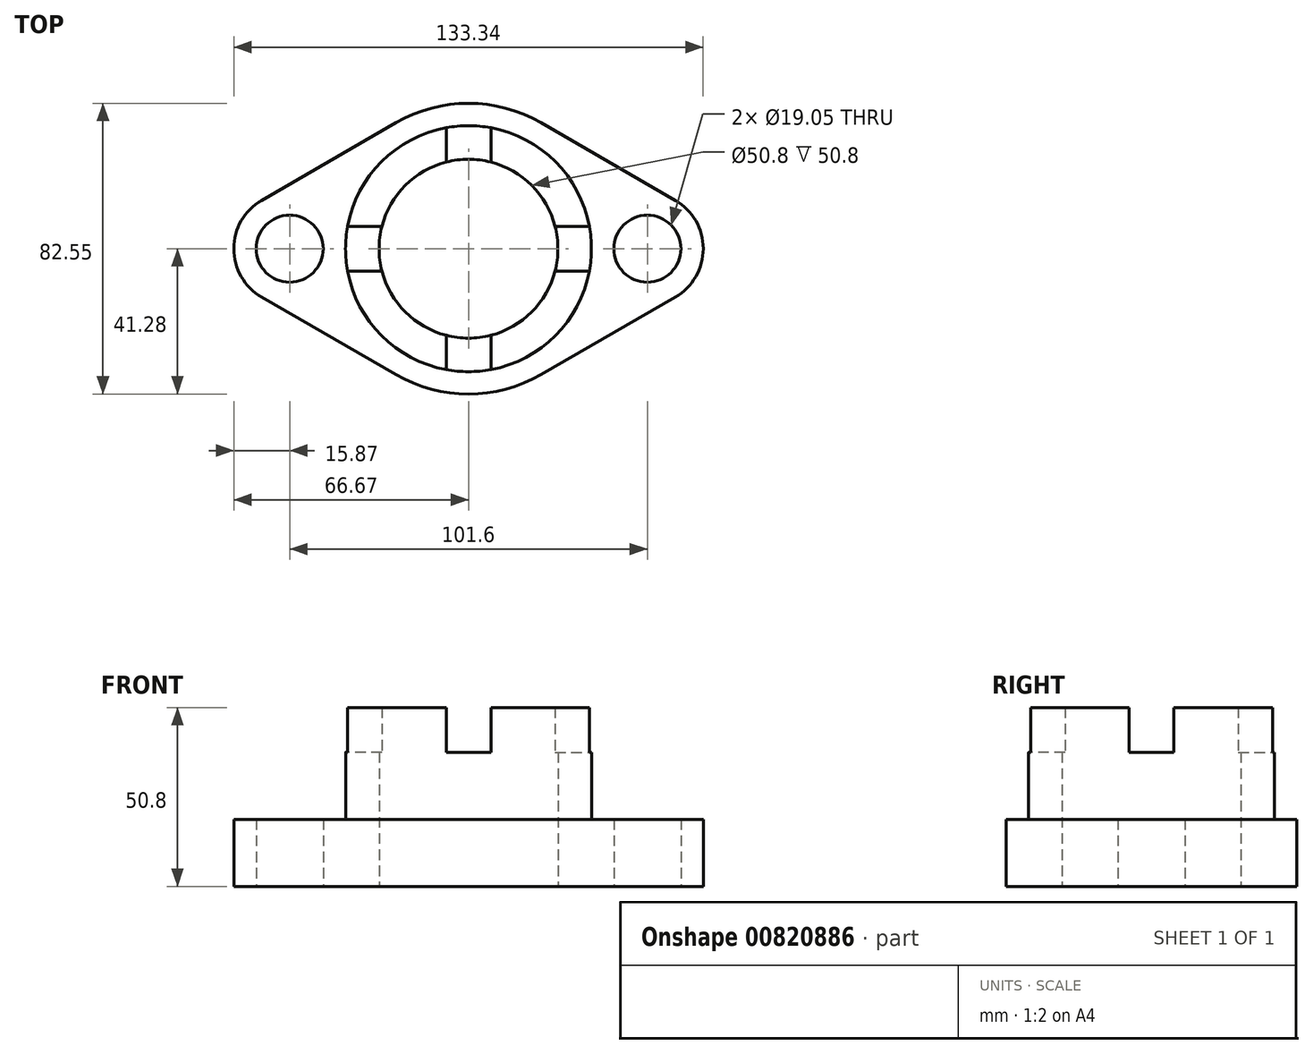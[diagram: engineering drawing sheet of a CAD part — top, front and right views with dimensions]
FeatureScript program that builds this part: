
annotation { "Feature Type Name" : "Feature", "Feature Type Description" : "" }
export const myFeature = defineFeature(function(context is Context, id is Id, definition is map)
    precondition{}
    {
        {
            var Q0;
            Q0=qCreatedBy(makeId("Top.planeOp"),FACE);
            var sketch = newSketch(context, id + "F0", { "sketchPlane" : qUnion([Q0])});
            skCircle(sketch, "E0", {"center": v(0, 0) * mm, "radius": 12.7 * mm});
            skCircle(sketch, "E1", {"center": v(-50.8, 0) * mm, "radius": 9.53 * mm});
            skCircle(sketch, "E2", {"center": v(0, 0) * mm, "radius": 25.4 * mm});
            skCircle(sketch, "E3", {"center": v(0, 0) * mm, "radius": 34.93 * mm});
            skLineSegment(sketch, "E4", {"start": v(-34.34, -6.35) * mm, "end": v(-24.6, -6.35) * mm});
            skLineSegment(sketch, "E5", {"start": v(-34.34, 6.35) * mm, "end": v(-24.6, 6.35) * mm});
            skLineSegment(sketch, "E6", {"start": v(-6.35, 34.34) * mm, "end": v(-6.35, 24.6) * mm});
            skLineSegment(sketch, "E7", {"start": v(-6.35, -34.34) * mm, "end": v(-6.35, -24.6) * mm});
            skLineSegment(sketch, "E8.MirrorCS", {"start": v(34.34, 6.35) * mm, "end": v(24.6, 6.35) * mm});
            skLineSegment(sketch, "E9.MirrorCS", {"start": v(6.35, -34.34) * mm, "end": v(6.35, -24.6) * mm});
            skLineSegment(sketch, "E10.MirrorCS", {"start": v(6.35, 34.34) * mm, "end": v(6.35, 24.6) * mm});
            skLineSegment(sketch, "E11.MirrorCS", {"start": v(34.34, -6.35) * mm, "end": v(24.6, -6.35) * mm});
            skCircle(sketch, "E12.MirrorC", {"center": v(50.8, 0) * mm, "radius": 9.53 * mm});
            skArc(sketch, "E13", {"start": v(58.74, -13.75) * mm, "mid": v(66.68, 0) * mm, "end": v(58.74, 13.75) * mm});
            skArc(sketch, "E14", {"start": v(-58.74, 13.75) * mm, "mid": v(-66.68, 0) * mm, "end": v(-58.74, -13.75) * mm});
            skLineSegment(sketch, "E15", {"start": v(-58.74, -13.75) * mm, "end": v(-20.64, -35.75) * mm});
            skLineSegment(sketch, "E16", {"start": v(-58.74, 13.75) * mm, "end": v(-20.64, 35.75) * mm});
            skLineSegment(sketch, "E17", {"start": v(20.64, -35.75) * mm, "end": v(58.74, -13.75) * mm});
            skLineSegment(sketch, "E18", {"start": v(20.64, 35.75) * mm, "end": v(58.74, 13.75) * mm});
            skArc(sketch, "E19.trimOffspring", {"start": v(-20.64, -35.75) * mm, "mid": v(0, -41.28) * mm, "end": v(20.64, -35.75) * mm});
            skArc(sketch, "E20.trimOffspring", {"start": v(20.64, 35.75) * mm, "mid": v(0, 41.28) * mm, "end": v(-20.64, 35.75) * mm});
            skPoint(sketch, "E21.end.orphan", {"position": v(0, -6.35) * mm});
            skSolve(sketch);
        }
        {
            var Q0;
            Q0 = qSketchRegion(id + "F0", true);
            extrude(context, id + "F1", {"entities" : qUnion([Q0]), "depth" : 19.05 * mm, "offsetDistance" : 25.4 * mm});
        }
        {
            var Q0;
            {var subQ0=sQuery(id+"F0.wireOp",EDGE,"E7");Q0=makeQuery(id+"F0.imprint","IMPRINT",FACE,{"disambiguationData":[TD([[makeQuery(id+"F0.imprint","IMPRINT",EDGE,{"derivedFrom":subQ0}),-1.0]])]});}
            var Q1;
            {var subQ0=sQuery(id+"F0.wireOp",EDGE,"E4");Q1=makeQuery(id+"F0.imprint","IMPRINT",FACE,{"disambiguationData":[TD([[makeQuery(id+"F0.imprint","IMPRINT",EDGE,{"derivedFrom":subQ0}),-1.0]])]});}
            var Q2;
            {var subQ0=sQuery(id+"F0.wireOp",EDGE,"E9.MirrorCS");Q2=makeQuery(id+"F0.imprint","IMPRINT",FACE,{"disambiguationData":[TD([[makeQuery(id+"F0.imprint","IMPRINT",EDGE,{"derivedFrom":subQ0}),-1.0]])]});}
            var Q3;
            Q3=makeQuery(id+"F0.imprint","IMPRINT",FACE,{"disambiguationData":[TD([[makeQuery(id+"F0.imprint","IMPRINT",EDGE,{"derivedFrom":sQuery(id+"F0.wireOp",EDGE,"E0")}),1.0]])]});
            var Q4;
            {var subQ0=sQuery(id+"F0.wireOp",EDGE,"E8.MirrorCS");Q4=makeQuery(id+"F0.imprint","IMPRINT",FACE,{"disambiguationData":[TD([[makeQuery(id+"F0.imprint","IMPRINT",EDGE,{"derivedFrom":subQ0}),1.0]])]});}
            var Q5;
            {var subQ0=sQuery(id+"F0.wireOp",EDGE,"E8.MirrorCS");Q5=makeQuery(id+"F0.imprint","IMPRINT",FACE,{"disambiguationData":[TD([[makeQuery(id+"F0.imprint","IMPRINT",EDGE,{"derivedFrom":subQ0}),-1.0]])]});}
            var Q6;
            {var subQ0=sQuery(id+"F0.wireOp",EDGE,"E4");Q6=makeQuery(id+"F0.imprint","IMPRINT",FACE,{"disambiguationData":[TD([[makeQuery(id+"F0.imprint","IMPRINT",EDGE,{"derivedFrom":subQ0}),1.0]])]});}
            var Q7;
            {var subQ0=sQuery(id+"F0.wireOp",EDGE,"E5");Q7=makeQuery(id+"F0.imprint","IMPRINT",FACE,{"disambiguationData":[TD([[makeQuery(id+"F0.imprint","IMPRINT",EDGE,{"derivedFrom":subQ0}),1.0]])]});}
            var Q8;
            {var subQ0=sQuery(id+"F0.wireOp",EDGE,"E6");Q8=makeQuery(id+"F0.imprint","IMPRINT",FACE,{"disambiguationData":[TD([[makeQuery(id+"F0.imprint","IMPRINT",EDGE,{"derivedFrom":subQ0}),1.0]])]});}
            extrude(context, id + "F2", {"entities" : qUnion([Q0, Q1, Q2, Q3, Q4, Q5, Q6, Q7, Q8]), "operationType" : NewBodyOperationType.ADD, "depth" : 38.1 * mm, "offsetDistance" : 25.4 * mm});
        }
        {
            var Q0;
            {var subQ0=sQuery(id+"F0.wireOp",EDGE,"E8.MirrorCS");Q0=makeQuery(id+"F0.imprint","IMPRINT",FACE,{"disambiguationData":[TD([[makeQuery(id+"F0.imprint","IMPRINT",EDGE,{"derivedFrom":subQ0}),-1.0]])]});}
            var Q1;
            {var subQ0=sQuery(id+"F0.wireOp",EDGE,"E9.MirrorCS");Q1=makeQuery(id+"F0.imprint","IMPRINT",FACE,{"disambiguationData":[TD([[makeQuery(id+"F0.imprint","IMPRINT",EDGE,{"derivedFrom":subQ0}),-1.0]])]});}
            var Q2;
            {var subQ0=sQuery(id+"F0.wireOp",EDGE,"E4");Q2=makeQuery(id+"F0.imprint","IMPRINT",FACE,{"disambiguationData":[TD([[makeQuery(id+"F0.imprint","IMPRINT",EDGE,{"derivedFrom":subQ0}),-1.0]])]});}
            var Q3;
            {var subQ0=sQuery(id+"F0.wireOp",EDGE,"E5");Q3=makeQuery(id+"F0.imprint","IMPRINT",FACE,{"disambiguationData":[TD([[makeQuery(id+"F0.imprint","IMPRINT",EDGE,{"derivedFrom":subQ0}),1.0]])]});}
            extrude(context, id + "F3", {"entities" : qUnion([Q0, Q1, Q2, Q3]), "operationType" : NewBodyOperationType.ADD, "depth" : 50.8 * mm, "offsetDistance" : 25.4 * mm});
        }
    });
